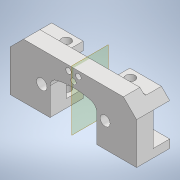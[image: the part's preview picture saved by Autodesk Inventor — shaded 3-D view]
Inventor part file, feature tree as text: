
AUTODESK INVENTOR PART (.ipt)
format: ipt  version: 2022 (Build 260153000, 153)  size: 223,744 bytes
history: native  units: in
note: dims shown in document units (in); Inventor stores cm internally (conversion verified against a paired STEP export)
features: reference x6, extrude x5, sketch x5, plane x4, other x3, fillet x1, mirror x1, projected_geometry x1
ambient origin geometry x8: Origin, YZ Plane, XZ Plane, XY Plane, X Axis, Y Axis, Z Axis, Center Point
bodies: Solid1 (feature_tree)
feature tree (26):
  extrude  "Extrusion1"  Depth=0.0039in
  plane  "Work Plane1"
  extrude  "Extrusion3"  Depth=0.0039in
  sketch  "Sketch4"  dims[d4=0.0039in d5=0.0039in]
  plane  "Work Plane2"
  extrude  "Extrusion4"  Depth=0.0039in
  extrude  "Extrusion5"  Depth=0.315in
  extrude  "Extrusion6"  Depth=0.0394in
  fillet  "Fillet2"  Radius=0.1181in
  plane  "Work Plane3"
  mirror  "Mirror1"
  sketch  "Sketch1"  dims[d0=0.0039in d1=0.0039in]
  reference  "Reference1"
  reference  "Reference2"
  reference  "Reference3"
  sketch  "Sketch3"  dims[d2=0.0039in d3=0.0039in]
  reference  "Reference4"
  projected_geometry  "Projected Loop2"
  sketch  "Sketch5"  dims[d7=1.5748in d9=0.315in]
  reference  "Reference5"
  sketch  "Sketch6"  dims[d10=0.1181in d11=0.1299in d12=0.1181in d13=45.0deg d14=0.3937in d15=0.0in d16=0.1969in d17=0.1299in d19=0.2756in d25=0.1969in d26=0.7874in d27=0.0in d28=0.0039in d29=0.3937in d30=0.0in d31=0.1181in d32=0.0in d33=0.0118in d34=0.0in d35=0.0in d36=0.0394in]
  reference  "Reference6"
  plane  "Work Plane4"
  other  "Linear Rail Assembly.iam"
  other  "Guide rod bottom stand (independent):1"
  other  "cantilever:1"
